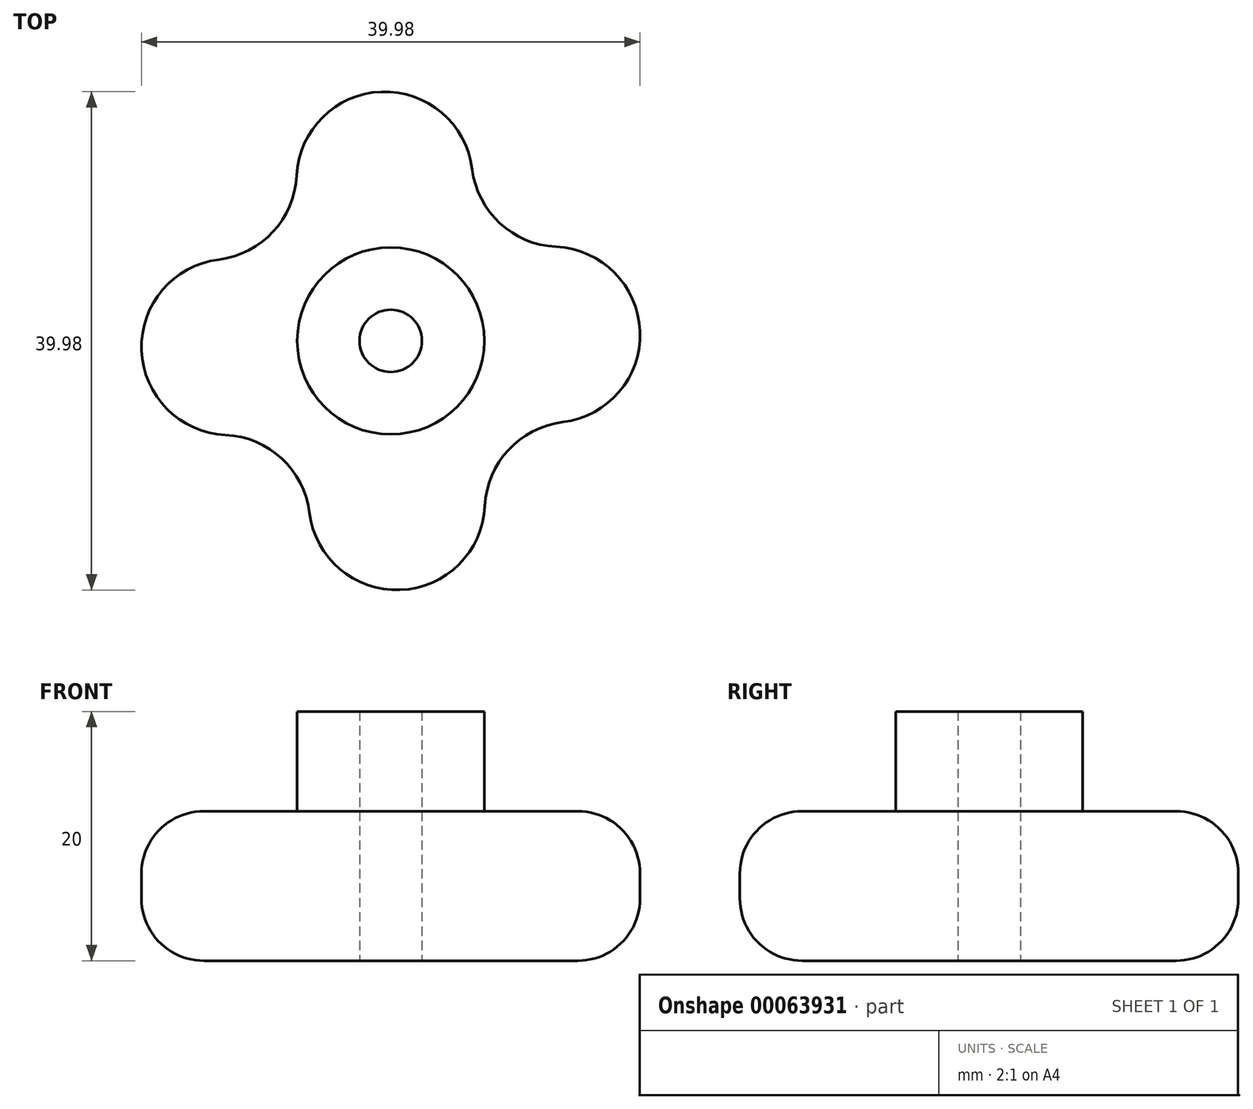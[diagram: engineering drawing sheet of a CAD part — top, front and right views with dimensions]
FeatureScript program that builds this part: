
annotation { "Feature Type Name" : "Feature", "Feature Type Description" : "" }
export const myFeature = defineFeature(function(context is Context, id is Id, definition is map)
    precondition{}
    {
        {
            var Q0;
            Q0=qCreatedBy(makeId("Top.planeOp"),FACE);
            var sketch = newSketch(context, id + "F0", { "sketchPlane" : qUnion([Q0])});
            skCircle(sketch, "E0", {"center": v(0, 0) * mm, "radius": 7.5 * mm});
            skCircle(sketch, "E1", {"center": v(0, 0) * mm, "radius": 20 * mm});
            skCircle(sketch, "E2.cCircle", {"center": v(0, 0) * mm, "radius": 20 * mm, "construction": true});
            skLineSegment(sketch, "E2.0", {"start": v(-13.6, -14.67) * mm, "end": v(-19.99, -0.76) * mm, "construction": true});
            skLineSegment(sketch, "E2.1", {"start": v(-19.99, -0.76) * mm, "end": v(-14.67, 13.6) * mm, "construction": true});
            skLineSegment(sketch, "E2.2", {"start": v(-14.67, 13.6) * mm, "end": v(-0.76, 19.99) * mm, "construction": true});
            skLineSegment(sketch, "E2.3", {"start": v(-0.76, 19.99) * mm, "end": v(13.6, 14.67) * mm, "construction": true});
            skLineSegment(sketch, "E2.4", {"start": v(13.6, 14.67) * mm, "end": v(19.99, 0.76) * mm, "construction": true});
            skLineSegment(sketch, "E2.5", {"start": v(19.99, 0.76) * mm, "end": v(14.67, -13.6) * mm, "construction": true});
            skLineSegment(sketch, "E2.6", {"start": v(14.67, -13.6) * mm, "end": v(0.76, -19.99) * mm, "construction": true});
            skLineSegment(sketch, "E2.7", {"start": v(0.76, -19.99) * mm, "end": v(-13.6, -14.67) * mm, "construction": true});
            skCircle(sketch, "E3", {"center": v(-13.6, -14.67) * mm, "radius": 7.13 * mm});
            skCircle(sketch, "E4", {"center": v(14.67, -13.6) * mm, "radius": 7.13 * mm});
            skCircle(sketch, "E5", {"center": v(13.6, 14.67) * mm, "radius": 7.13 * mm});
            skCircle(sketch, "E6", {"center": v(-14.67, 13.6) * mm, "radius": 7.13 * mm});
            skLineSegment(sketch, "E7", {"start": v(0, 0) * mm, "end": v(0.76, -19.99) * mm, "construction": true});
            skLineSegment(sketch, "E8", {"start": v(0, 0) * mm, "end": v(19.99, 0.76) * mm, "construction": true});
            skLineSegment(sketch, "E9", {"start": v(0, 0) * mm, "end": v(-0.76, 19.99) * mm, "construction": true});
            skLineSegment(sketch, "E10", {"start": v(-19.99, -0.76) * mm, "end": v(0, 0) * mm, "construction": true});
            skCircle(sketch, "E11", {"center": v(0.49, -12.92) * mm, "radius": 7.07 * mm});
            skCircle(sketch, "E12", {"center": v(12.92, 0.49) * mm, "radius": 7.07 * mm});
            skCircle(sketch, "E13", {"center": v(-0.49, 12.92) * mm, "radius": 7.07 * mm});
            skCircle(sketch, "E14", {"center": v(-12.92, -0.49) * mm, "radius": 7.07 * mm});
            skCircle(sketch, "E15", {"center": v(0, 0) * mm, "radius": 2.5 * mm});
            skSolve(sketch);
        }
        {
            var Q0;
            {var subQ1=sQuery(id+"F0.wireOp",EDGE,"E0");var subQ8=sQuery(id+"F0.wireOp",EDGE,"E13");var subQ11=makeQuery(id+"F0.imprint","INTERSECT",VERTEX,{"disambiguationData":[OD(0.0)],"derivedFrom":[subQ1,subQ8]});Q0=makeQuery(id+"F0.imprint","IMPRINT",FACE,{"disambiguationData":[TD([[makeQuery(id+"F0.imprint","IMPRINT",EDGE,{"disambiguationData":[TD([[subQ11,1.0]])],"derivedFrom":subQ1}),1.0]])]});}
            var Q1;
            {var subQ0=sQuery(id+"F0.wireOp",EDGE,"E13");var subQ1=sQuery(id+"F0.wireOp",EDGE,"E0");var subQ2=makeQuery(id+"F0.imprint","INTERSECT",VERTEX,{"disambiguationData":[OD(0.0)],"derivedFrom":[subQ1,subQ0]});Q1=makeQuery(id+"F0.imprint","IMPRINT",FACE,{"disambiguationData":[TD([[makeQuery(id+"F0.imprint","IMPRINT",EDGE,{"disambiguationData":[TD([[subQ2,-1.0]])],"derivedFrom":subQ1}),1.0]])]});}
            var Q2;
            {var subQ0=sQuery(id+"F0.wireOp",EDGE,"E12");var subQ1=sQuery(id+"F0.wireOp",EDGE,"E0");var subQ2=makeQuery(id+"F0.imprint","INTERSECT",VERTEX,{"disambiguationData":[OD(0.0)],"derivedFrom":[subQ1,subQ0]});Q2=makeQuery(id+"F0.imprint","IMPRINT",FACE,{"disambiguationData":[TD([[makeQuery(id+"F0.imprint","IMPRINT",EDGE,{"disambiguationData":[TD([[subQ2,1.0]])],"derivedFrom":subQ1}),1.0]])]});}
            var Q3;
            {var subQ0=sQuery(id+"F0.wireOp",EDGE,"E11");var subQ1=sQuery(id+"F0.wireOp",EDGE,"E0");var subQ2=makeQuery(id+"F0.imprint","INTERSECT",VERTEX,{"disambiguationData":[OD(0.0)],"derivedFrom":[subQ1,subQ0]});Q3=makeQuery(id+"F0.imprint","IMPRINT",FACE,{"disambiguationData":[TD([[makeQuery(id+"F0.imprint","IMPRINT",EDGE,{"disambiguationData":[TD([[subQ2,-1.0]])],"derivedFrom":subQ1}),1.0]])]});}
            var Q4;
            {var subQ0=sQuery(id+"F0.wireOp",EDGE,"E14");var subQ1=sQuery(id+"F0.wireOp",EDGE,"E0");var subQ2=makeQuery(id+"F0.imprint","INTERSECT",VERTEX,{"disambiguationData":[OD(0.0)],"derivedFrom":[subQ1,subQ0]});Q4=makeQuery(id+"F0.imprint","IMPRINT",FACE,{"disambiguationData":[TD([[makeQuery(id+"F0.imprint","IMPRINT",EDGE,{"disambiguationData":[TD([[subQ2,-1.0]])],"derivedFrom":subQ1}),1.0]])]});}
            extrude(context, id + "F1", {"entities" : qUnion([Q0, Q1, Q2, Q3, Q4]), "depth" : 20 * mm});
        }
        {
            var Q0;
            {var subQ0=sQuery(id+"F0.wireOp",EDGE,"E14");var subQ1=sQuery(id+"F0.wireOp",EDGE,"E0");var subQ2=makeQuery(id+"F0.imprint","INTERSECT",VERTEX,{"disambiguationData":[OD(1.0)],"derivedFrom":[subQ1,subQ0]});Q0=makeQuery(id+"F0.imprint","IMPRINT",FACE,{"disambiguationData":[TD([[makeQuery(id+"F0.imprint","IMPRINT",EDGE,{"disambiguationData":[TD([[subQ2,-1.0]])],"derivedFrom":subQ1}),-1.0]])]});}
            var Q1;
            {var subQ0=sQuery(id+"F0.wireOp",EDGE,"E12");var subQ1=sQuery(id+"F0.wireOp",EDGE,"E0");var subQ4=makeQuery(id+"F0.imprint","INTERSECT",VERTEX,{"disambiguationData":[OD(0.0)],"derivedFrom":[subQ1,subQ0]});Q1=makeQuery(id+"F0.imprint","IMPRINT",FACE,{"disambiguationData":[TD([[makeQuery(id+"F0.imprint","IMPRINT",EDGE,{"disambiguationData":[TD([[subQ4,1.0]])],"derivedFrom":subQ1}),-1.0]])]});}
            var Q2;
            {var subQ0=sQuery(id+"F0.wireOp",EDGE,"E11");var subQ1=sQuery(id+"F0.wireOp",EDGE,"E0");var subQ2=makeQuery(id+"F0.imprint","INTERSECT",VERTEX,{"disambiguationData":[OD(1.0)],"derivedFrom":[subQ1,subQ0]});Q2=makeQuery(id+"F0.imprint","IMPRINT",FACE,{"disambiguationData":[TD([[makeQuery(id+"F0.imprint","IMPRINT",EDGE,{"disambiguationData":[TD([[subQ2,-1.0]])],"derivedFrom":subQ1}),-1.0]])]});}
            var Q3;
            {var subQ1=sQuery(id+"F0.wireOp",EDGE,"E0");var subQ8=sQuery(id+"F0.wireOp",EDGE,"E13");var subQ11=makeQuery(id+"F0.imprint","INTERSECT",VERTEX,{"disambiguationData":[OD(0.0)],"derivedFrom":[subQ1,subQ8]});Q3=makeQuery(id+"F0.imprint","IMPRINT",FACE,{"disambiguationData":[TD([[makeQuery(id+"F0.imprint","IMPRINT",EDGE,{"disambiguationData":[TD([[subQ11,1.0]])],"derivedFrom":subQ1}),1.0]])]});}
            var Q4;
            {var subQ0=sQuery(id+"F0.wireOp",EDGE,"E12");var subQ1=sQuery(id+"F0.wireOp",EDGE,"E0");var subQ2=makeQuery(id+"F0.imprint","INTERSECT",VERTEX,{"disambiguationData":[OD(0.0)],"derivedFrom":[subQ1,subQ0]});Q4=makeQuery(id+"F0.imprint","IMPRINT",FACE,{"disambiguationData":[TD([[makeQuery(id+"F0.imprint","IMPRINT",EDGE,{"disambiguationData":[TD([[subQ2,1.0]])],"derivedFrom":subQ1}),1.0]])]});}
            var Q5;
            {var subQ0=sQuery(id+"F0.wireOp",EDGE,"E11");var subQ4=sQuery(id+"F0.wireOp",EDGE,"E0");var subQ5=makeQuery(id+"F0.imprint","INTERSECT",VERTEX,{"disambiguationData":[OD(0.0)],"derivedFrom":[subQ4,subQ0]});Q5=makeQuery(id+"F0.imprint","IMPRINT",FACE,{"disambiguationData":[TD([[makeQuery(id+"F0.imprint","IMPRINT",EDGE,{"disambiguationData":[TD([[subQ5,-1.0]])],"derivedFrom":subQ4}),-1.0]])]});}
            var Q6;
            {var subQ0=sQuery(id+"F0.wireOp",EDGE,"E13");var subQ1=sQuery(id+"F0.wireOp",EDGE,"E0");var subQ2=makeQuery(id+"F0.imprint","INTERSECT",VERTEX,{"disambiguationData":[OD(0.0)],"derivedFrom":[subQ1,subQ0]});Q6=makeQuery(id+"F0.imprint","IMPRINT",FACE,{"disambiguationData":[TD([[makeQuery(id+"F0.imprint","IMPRINT",EDGE,{"disambiguationData":[TD([[subQ2,1.0]])],"derivedFrom":subQ1}),-1.0]])]});}
            var Q7;
            {var subQ0=sQuery(id+"F0.wireOp",EDGE,"E13");var subQ4=sQuery(id+"F0.wireOp",EDGE,"E0");var subQ5=makeQuery(id+"F0.imprint","INTERSECT",VERTEX,{"disambiguationData":[OD(0.0)],"derivedFrom":[subQ4,subQ0]});Q7=makeQuery(id+"F0.imprint","IMPRINT",FACE,{"disambiguationData":[TD([[makeQuery(id+"F0.imprint","IMPRINT",EDGE,{"disambiguationData":[TD([[subQ5,-1.0]])],"derivedFrom":subQ4}),-1.0]])]});}
            var Q8;
            {var subQ0=sQuery(id+"F0.wireOp",EDGE,"E13");var subQ1=sQuery(id+"F0.wireOp",EDGE,"E0");var subQ2=makeQuery(id+"F0.imprint","INTERSECT",VERTEX,{"disambiguationData":[OD(1.0)],"derivedFrom":[subQ1,subQ0]});Q8=makeQuery(id+"F0.imprint","IMPRINT",FACE,{"disambiguationData":[TD([[makeQuery(id+"F0.imprint","IMPRINT",EDGE,{"disambiguationData":[TD([[subQ2,-1.0]])],"derivedFrom":subQ1}),-1.0]])]});}
            var Q9;
            {var subQ0=sQuery(id+"F0.wireOp",EDGE,"E14");var subQ4=sQuery(id+"F0.wireOp",EDGE,"E0");var subQ5=makeQuery(id+"F0.imprint","INTERSECT",VERTEX,{"disambiguationData":[OD(0.0)],"derivedFrom":[subQ4,subQ0]});Q9=makeQuery(id+"F0.imprint","IMPRINT",FACE,{"disambiguationData":[TD([[makeQuery(id+"F0.imprint","IMPRINT",EDGE,{"disambiguationData":[TD([[subQ5,-1.0]])],"derivedFrom":subQ4}),-1.0]])]});}
            var Q10;
            {var subQ0=sQuery(id+"F0.wireOp",EDGE,"E14");var subQ1=sQuery(id+"F0.wireOp",EDGE,"E0");var subQ2=makeQuery(id+"F0.imprint","INTERSECT",VERTEX,{"disambiguationData":[OD(0.0)],"derivedFrom":[subQ1,subQ0]});Q10=makeQuery(id+"F0.imprint","IMPRINT",FACE,{"disambiguationData":[TD([[makeQuery(id+"F0.imprint","IMPRINT",EDGE,{"disambiguationData":[TD([[subQ2,-1.0]])],"derivedFrom":subQ1}),1.0]])]});}
            var Q11;
            {var subQ0=sQuery(id+"F0.wireOp",EDGE,"E11");var subQ1=sQuery(id+"F0.wireOp",EDGE,"E0");var subQ2=makeQuery(id+"F0.imprint","INTERSECT",VERTEX,{"disambiguationData":[OD(0.0)],"derivedFrom":[subQ1,subQ0]});Q11=makeQuery(id+"F0.imprint","IMPRINT",FACE,{"disambiguationData":[TD([[makeQuery(id+"F0.imprint","IMPRINT",EDGE,{"disambiguationData":[TD([[subQ2,-1.0]])],"derivedFrom":subQ1}),1.0]])]});}
            var Q12;
            {var subQ0=sQuery(id+"F0.wireOp",EDGE,"E13");var subQ1=sQuery(id+"F0.wireOp",EDGE,"E0");var subQ2=makeQuery(id+"F0.imprint","INTERSECT",VERTEX,{"disambiguationData":[OD(0.0)],"derivedFrom":[subQ1,subQ0]});Q12=makeQuery(id+"F0.imprint","IMPRINT",FACE,{"disambiguationData":[TD([[makeQuery(id+"F0.imprint","IMPRINT",EDGE,{"disambiguationData":[TD([[subQ2,-1.0]])],"derivedFrom":subQ1}),1.0]])]});}
            extrude(context, id + "F2", {"entities" : qUnion([Q0, Q1, Q2, Q3, Q4, Q5, Q6, Q7, Q8, Q9, Q10, Q11, Q12]), "operationType" : NewBodyOperationType.ADD, "depth" : 12 * mm});
        }
        {
            var Q0;
            Q0=makeQuery(id+"F2.opExtrude","CAP_EDGE",EDGE,{"disambiguationData":[OSD([sQuery(id+"F0.wireOp",EDGE,"E14")])],"isStart":false});
            var Q1;
            Q1=makeQuery(id+"F2.opExtrude","CAP_EDGE",EDGE,{"disambiguationData":[OSD([sQuery(id+"F0.wireOp",EDGE,"E14")])],"isStart":true});
            fillet(context, id + "F3", {"entities" : qUnion([Q0, Q1]), "radius" : 5 * mm, "tangentPropagation" : true, "allowEdgeOverflow" : false});
        }
    });
